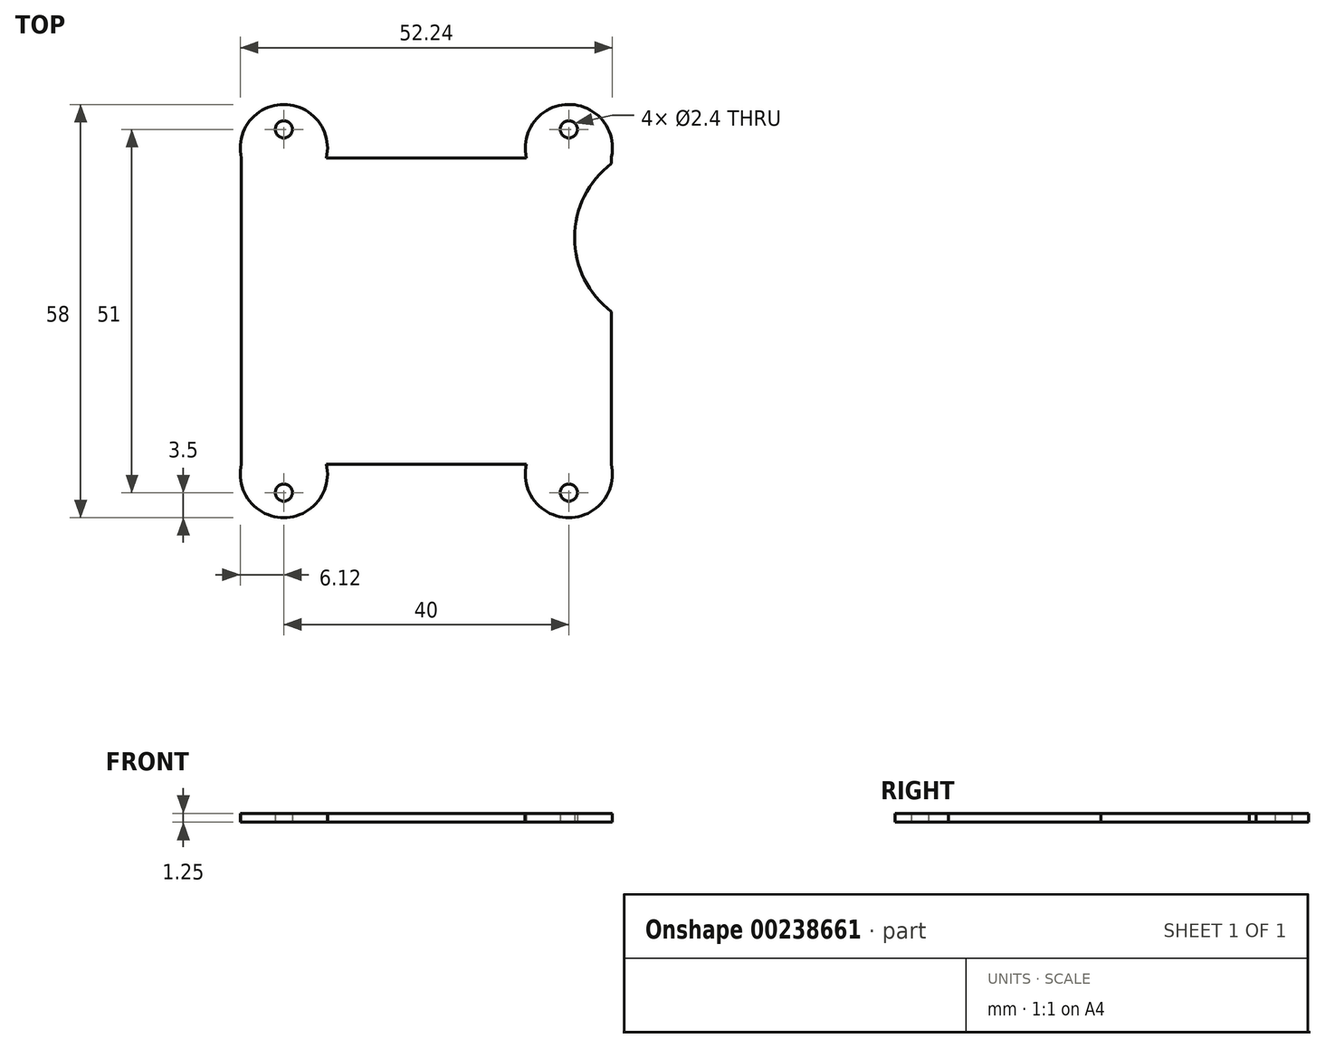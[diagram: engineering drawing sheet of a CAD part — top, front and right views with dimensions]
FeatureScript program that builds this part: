
annotation { "Feature Type Name" : "Feature", "Feature Type Description" : "" }
export const myFeature = defineFeature(function(context is Context, id is Id, definition is map)
    precondition{}
    {
        {
            var Q0;
            Q0=qCreatedBy(makeId("Top.planeOp"),FACE);
            var sketch = newSketch(context, id + "F0", { "sketchPlane" : qUnion([Q0])});
            skLineSegment(sketch, "E0.bottom", {"start": v(20, 25.5) * mm, "end": v(-20, 25.5) * mm, "construction": true});
            skLineSegment(sketch, "E0.top", {"start": v(20, -25.5) * mm, "end": v(-20, -25.5) * mm, "construction": true});
            skLineSegment(sketch, "E0.left", {"start": v(20, 25.5) * mm, "end": v(20, -25.5) * mm, "construction": true});
            skLineSegment(sketch, "E0.right", {"start": v(-20, 25.5) * mm, "end": v(-20, -25.5) * mm, "construction": true});
            skPoint(sketch, "E0.middle", {"position": v(0, 0) * mm});
            skCircle(sketch, "E1", {"center": v(20, 25.5) * mm, "radius": 1.2 * mm});
            skArc(sketch, "E2", {"start": v(26, 21.64) * mm, "mid": v(19.93, 29) * mm, "end": v(14.03, 21.5) * mm});
            skArc(sketch, "E3.MirrorC", {"start": v(-25.97, 21.5) * mm, "mid": v(-20, 29) * mm, "end": v(-14.03, 21.5) * mm});
            skCircle(sketch, "E4.MirrorC", {"center": v(-20, 25.5) * mm, "radius": 1.2 * mm});
            skCircle(sketch, "E5.MirrorC", {"center": v(-20, -25.5) * mm, "radius": 1.2 * mm});
            skArc(sketch, "E6.MirrorC", {"start": v(-25.97, -21.5) * mm, "mid": v(-20, -29) * mm, "end": v(-14.03, -21.5) * mm});
            skArc(sketch, "E7.MirrorC", {"start": v(25.97, -21.5) * mm, "mid": v(20, -29) * mm, "end": v(14.03, -21.5) * mm});
            skCircle(sketch, "E8.MirrorC", {"center": v(20, -25.5) * mm, "radius": 1.2 * mm});
            skLineSegment(sketch, "E9.bottom", {"start": v(26, 21.5) * mm, "end": v(25.97, 21.5) * mm});
            skLineSegment(sketch, "E9.top", {"start": v(26, -21.5) * mm, "end": v(25.97, -21.5) * mm});
            skLineSegment(sketch, "E9.left", {"start": v(26, 21.64) * mm, "end": v(26, 20.7) * mm});
            skLineSegment(sketch, "E9.right", {"start": v(-26, 21.5) * mm, "end": v(-26, -21.5) * mm});
            skLineSegment(sketch, "E10.trimOffspring", {"start": v(-25.97, 21.5) * mm, "end": v(-26, 21.5) * mm});
            skLineSegment(sketch, "E11.trimOffspring", {"start": v(14.03, 21.5) * mm, "end": v(-14.03, 21.5) * mm});
            skLineSegment(sketch, "E12.trimOffspring", {"start": v(14.03, -21.5) * mm, "end": v(-14.03, -21.5) * mm});
            skLineSegment(sketch, "E13.trimOffspring", {"start": v(-25.97, -21.5) * mm, "end": v(-26, -21.5) * mm});
            skArc(sketch, "E14", {"start": v(26, 20.7) * mm, "mid": v(20.8, 10.3) * mm, "end": v(26, -0.1) * mm});
            skLineSegment(sketch, "E15.trimOffspring", {"start": v(26, -0.1) * mm, "end": v(26, -21.5) * mm});
            skSolve(sketch);
        }
        {
            var Q0;
            Q0 = qSketchRegion(id + "F0", true);
            extrude(context, id + "F1", {"entities" : qUnion([Q0]), "depth" : 1.25 * mm});
        }
    });
